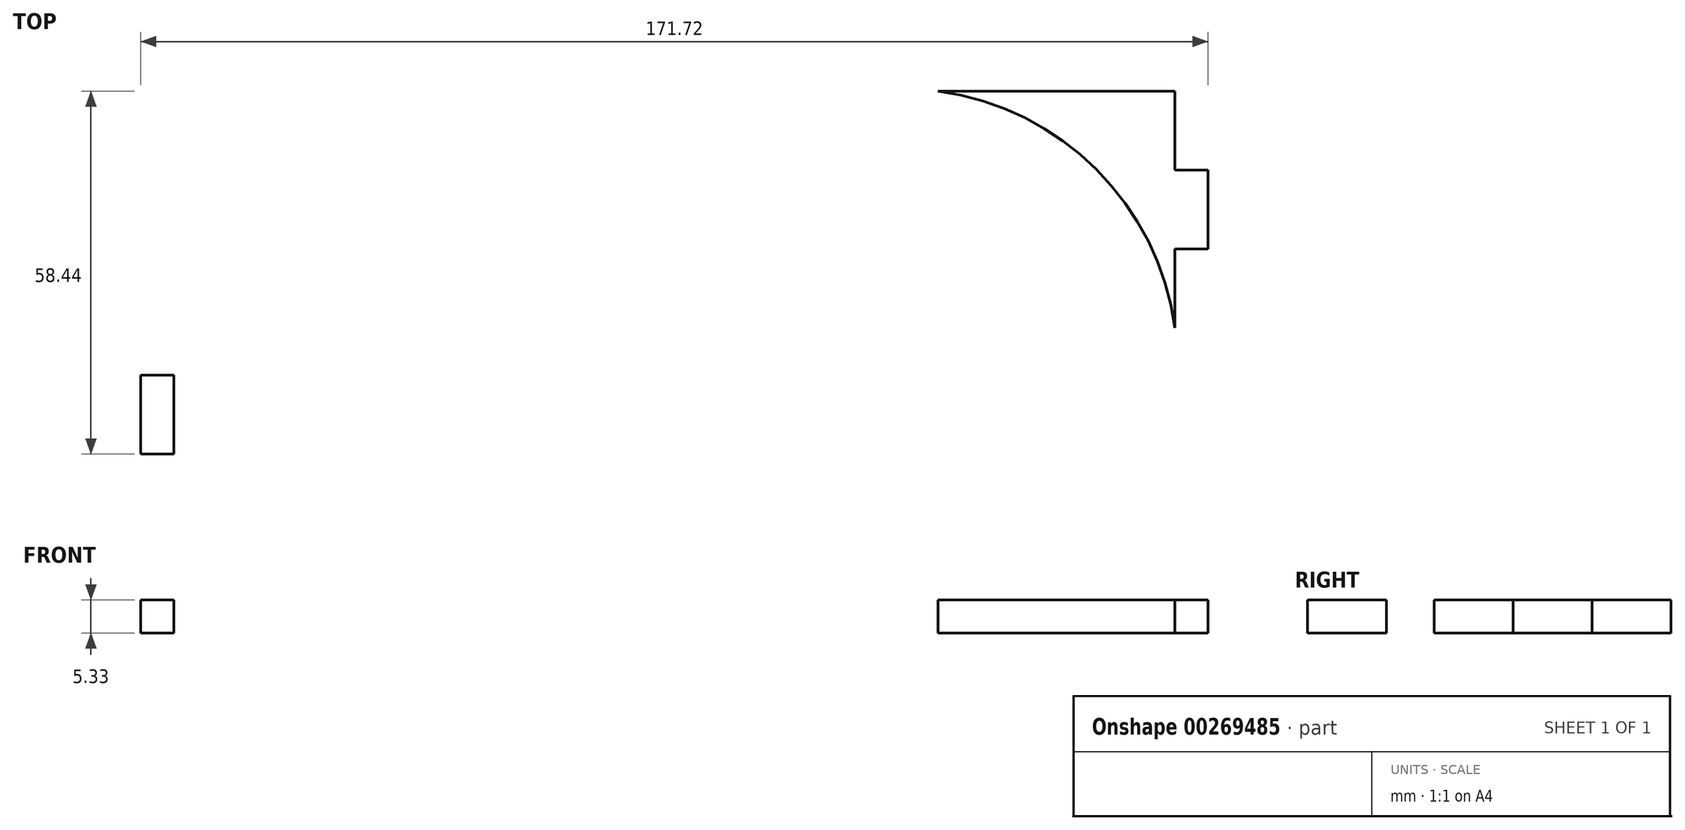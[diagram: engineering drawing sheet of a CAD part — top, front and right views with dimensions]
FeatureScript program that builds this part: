
annotation { "Feature Type Name" : "Feature", "Feature Type Description" : "" }
export const myFeature = defineFeature(function(context is Context, id is Id, definition is map)
    precondition{}
    {
        {
            var Q0;
            Q0=qCreatedBy(makeId("Top.planeOp"),FACE);
            var sketch = newSketch(context, id + "F0", { "sketchPlane" : qUnion([Q0])});
            skLineSegment(sketch, "E0.bottom", {"start": v(-85.27, 71.14) * mm, "end": v(74.34, 71.14) * mm});
            skLineSegment(sketch, "E0.top", {"start": v(-85.27, -68.98) * mm, "end": v(74.34, -68.98) * mm});
            skLineSegment(sketch, "E0.left", {"start": v(-85.27, 71.14) * mm, "end": v(-85.27, -68.98) * mm});
            skLineSegment(sketch, "E0.right", {"start": v(74.34, 71.14) * mm, "end": v(74.34, -68.98) * mm});
            skCircle(sketch, "E1", {"center": v(26.71, 23.52) * mm, "radius": 47.63 * mm});
            skArc(sketch, "E2", {"start": v(74.34, 33.04) * mm, "mid": v(61.72, 58.53) * mm, "end": v(36.24, 71.14) * mm});
            skLineSegment(sketch, "E3", {"start": v(26.71, 71.14) * mm, "end": v(26.71, 75) * mm});
            skLineSegment(sketch, "E4.bottom", {"start": v(48.94, 71.14) * mm, "end": v(61.64, 71.14) * mm});
            skLineSegment(sketch, "E4.top", {"start": v(48.94, 76.48) * mm, "end": v(61.64, 76.48) * mm});
            skLineSegment(sketch, "E4.left", {"start": v(48.94, 71.14) * mm, "end": v(48.94, 76.48) * mm});
            skLineSegment(sketch, "E4.right", {"start": v(61.64, 71.14) * mm, "end": v(61.64, 76.48) * mm});
            skLineSegment(sketch, "E5.bottom", {"start": v(74.34, 58.44) * mm, "end": v(79.67, 58.44) * mm});
            skLineSegment(sketch, "E5.top", {"start": v(74.34, 45.74) * mm, "end": v(79.67, 45.74) * mm});
            skLineSegment(sketch, "E5.left", {"start": v(74.34, 58.44) * mm, "end": v(74.34, 45.74) * mm});
            skLineSegment(sketch, "E5.right", {"start": v(79.67, 58.44) * mm, "end": v(79.67, 45.74) * mm});
            skSolve(sketch);
        }
        {
            var Q0;
            Q0=makeQuery(id+"F0.imprint","IMPRINT",FACE,{"disambiguationData":[TD([[makeQuery(id+"F0.imprint","IMPRINT",EDGE,{"derivedFrom":sQuery(id+"F0.wireOp",EDGE,"E4.bottom")}),1.0]])]});
            var Q1;
            Q1=makeQuery(id+"F0.imprint","IMPRINT",FACE,{"disambiguationData":[TD([[makeQuery(id+"F0.imprint","IMPRINT",EDGE,{"derivedFrom":sQuery(id+"F0.wireOp",EDGE,"E5.bottom")}),-1.0]])]});
            var Q2;
            {var subQ0=sQuery(id+"F0.wireOp",EDGE,"E2");Q2=makeQuery(id+"F0.imprint","IMPRINT",FACE,{"disambiguationData":[TD([[makeQuery(id+"F0.imprint","IMPRINT",EDGE,{"derivedFrom":subQ0}),-1.0]])]});}
            extrude(context, id + "F1", {"entities" : qUnion([Q0, Q1, Q2]), "depth" : 5.33 * mm});
        }
        {
            var Q0;
            Q0=qCreatedBy(makeId("Top.planeOp"),FACE);
            var sketch = newSketch(context, id + "F2", { "sketchPlane" : qUnion([Q0])});
            skLineSegment(sketch, "E6.bottom", {"start": v(-130.15, 38.1) * mm, "end": v(-92.05, 38.1) * mm});
            skLineSegment(sketch, "E6.top", {"start": v(-130.15, 0) * mm, "end": v(-92.05, 0) * mm});
            skLineSegment(sketch, "E6.left", {"start": v(-130.15, 38.1) * mm, "end": v(-130.15, 0) * mm});
            skLineSegment(sketch, "E6.right", {"start": v(-92.05, 38.1) * mm, "end": v(-92.05, 0) * mm});
            skLineSegment(sketch, "E7.bottom", {"start": v(-117.45, 38.1) * mm, "end": v(-104.75, 38.1) * mm});
            skLineSegment(sketch, "E7.top", {"start": v(-117.45, 43.43) * mm, "end": v(-104.75, 43.43) * mm});
            skLineSegment(sketch, "E7.left", {"start": v(-117.45, 38.1) * mm, "end": v(-117.45, 43.43) * mm});
            skLineSegment(sketch, "E7.right", {"start": v(-104.75, 38.1) * mm, "end": v(-104.75, 43.43) * mm});
            skLineSegment(sketch, "E8.bottom", {"start": v(-92.05, 25.4) * mm, "end": v(-86.72, 25.4) * mm});
            skLineSegment(sketch, "E8.top", {"start": v(-92.05, 12.7) * mm, "end": v(-86.72, 12.7) * mm});
            skLineSegment(sketch, "E8.left", {"start": v(-92.05, 25.4) * mm, "end": v(-92.05, 12.7) * mm});
            skLineSegment(sketch, "E8.right", {"start": v(-86.72, 25.4) * mm, "end": v(-86.72, 12.7) * mm});
            skLineSegment(sketch, "E9", {"start": v(-130.15, 38.1) * mm, "end": v(-92.05, 0) * mm});
            skSolve(sketch);
        }
        {
            var Q0;
            {var subQ4=sQuery(id+"F2.wireOp",EDGE,"E7.bottom");Q0=makeQuery(id+"F2.imprint","IMPRINT",FACE,{"disambiguationData":[TD([[makeQuery(id+"F2.imprint","IMPRINT",EDGE,{"derivedFrom":subQ4}),-1.0]])]});}
            var Q1;
            Q1=makeQuery(id+"F2.imprint","IMPRINT",FACE,{"disambiguationData":[TD([[makeQuery(id+"F2.imprint","IMPRINT",EDGE,{"derivedFrom":sQuery(id+"F2.wireOp",EDGE,"E7.bottom")}),1.0]])]});
            var Q2;
            Q2=makeQuery(id+"F2.imprint","IMPRINT",FACE,{"disambiguationData":[TD([[makeQuery(id+"F2.imprint","IMPRINT",EDGE,{"derivedFrom":sQuery(id+"F2.wireOp",EDGE,"E8.bottom")}),-1.0]])]});
            extrude(context, id + "F3", {"entities" : qUnion([Q0, Q1, Q2]), "depth" : 5.33 * mm});
        }
    });
